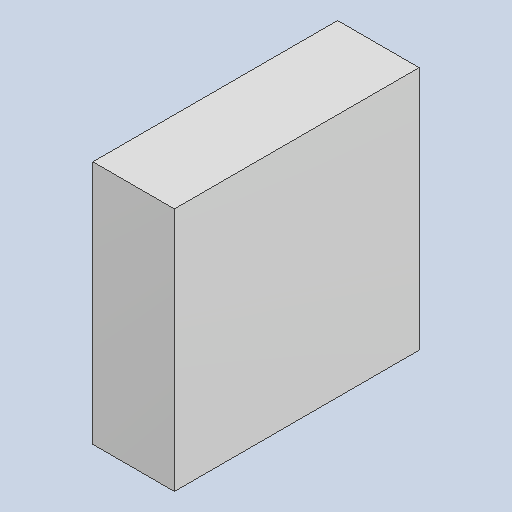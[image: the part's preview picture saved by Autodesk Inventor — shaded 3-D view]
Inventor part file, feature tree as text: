
AUTODESK INVENTOR PART (.ipt)
format: ipt  version: 2023.4 (Build 274418000, 418)  size: 81,408 bytes
history: native  units: mm
features: extrude x1
ambient origin geometry x8: Origin, YZ Plane, XZ Plane, XY Plane, X Axis, Y Axis, Z Axis, Center Point
bodies: Solid1 (feature_tree)
feature tree (1):
  extrude  "Extruded_20"  [1 undecoded]
note: 1 required parameter value undecoded (feature->parameter linkage not recoverable at this tier; creation-order binding heuristic only, values carry confidence <= 0.55)
